# Revit family: BM0006781_Barra Savona
name_source: partatom
category: Furniture
units: mm (PartAtom-declared; Revit-internal decimal feet)

## family parameters
Always vertical = Yes
Cut with Voids When Loaded = No
OmniClass Number = 23.40.20.00
OmniClass Title = General Furniture and Specialties
Room Calculation Point = No
Shared = No
Work Plane-Based = No

## types (1)
- BM0006781_Barra Savona
    Alto = 1000 mm  [stored 3.28084 ft]
    Ancho = 1500 mm  [stored 4.92126 ft]
    Carga máxima = 66,8 kg
    Densidad = 15 mm 670 kg./m^3
    Description = La mejor opción para ampliar la cocina e integrarla al
área social, práctico mueble que hace juego con la cocina
y alacena SAVONA, puede ser utilizada como comedor auxiliar
o principal, además cuenta con amplios gabinetes y repisas
que incrementan la capacidad de almacenamiento y un práctico espacio para organizar las botellas de vino
    Material = Corona_Madera_Coñac
    Peso Neto aproximado = 66,4 kg
    Profundidad = 600 mm  [stored 1.9685 ft]
    Referencia = BM0006781
    Resistencia a la humedad = Resistencia a la humedad
    URL = https://corona.co

note: [stored X ft] marks values corroborated as IEEE doubles in the binary element streams (Revit-internal decimal feet)

## geometry (parser evidence)
native form markers: Sweep x6
no freeform markers — native parametric forms only
